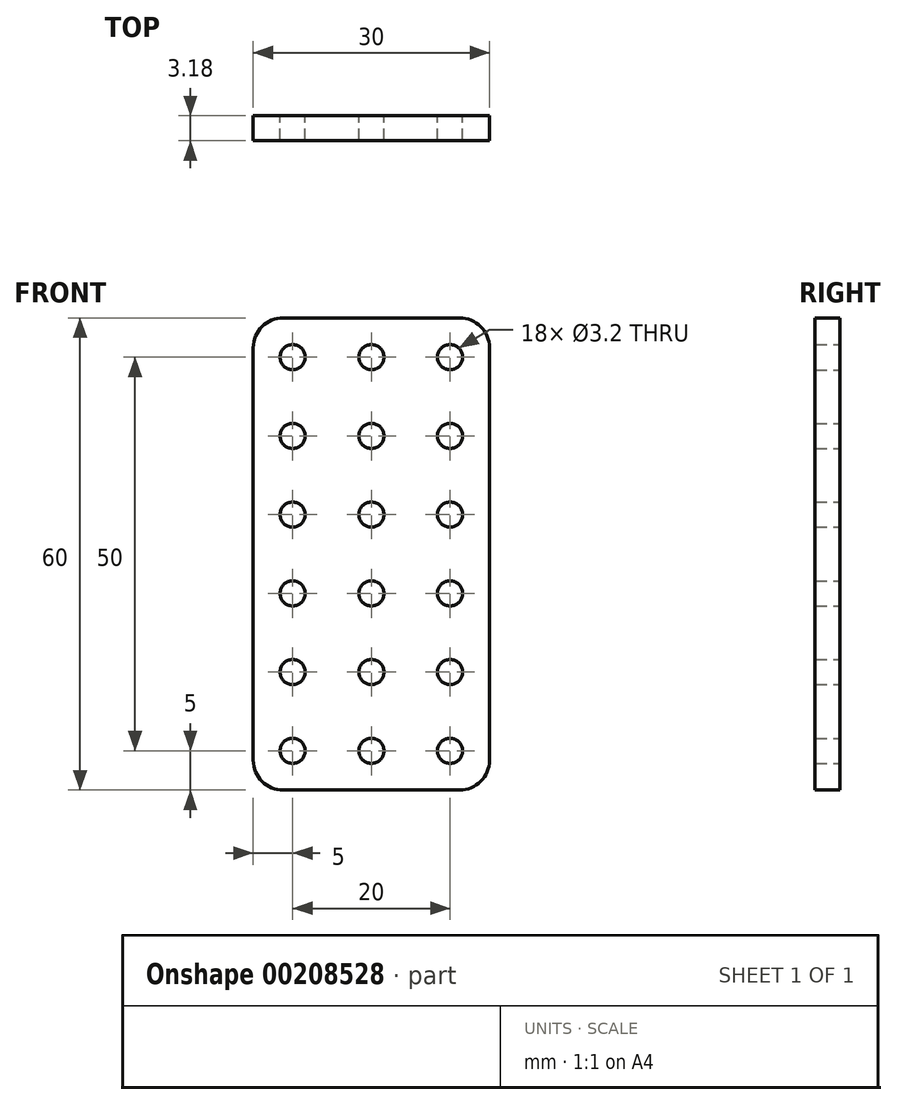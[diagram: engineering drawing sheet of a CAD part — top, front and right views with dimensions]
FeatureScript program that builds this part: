
annotation { "Feature Type Name" : "Feature", "Feature Type Description" : "" }
export const myFeature = defineFeature(function(context is Context, id is Id, definition is map)
    precondition{}
    {
        {
            var Q0;
            Q0=qCreatedBy(makeId("Front.planeOp"),FACE);
            var sketch = newSketch(context, id + "F0", { "sketchPlane" : qUnion([Q0])});
            skLineSegment(sketch, "E0.bottom", {"start": v(3.8, 0) * mm, "end": v(26.19, 0) * mm});
            skLineSegment(sketch, "E0.top", {"start": v(3.81, -60) * mm, "end": v(26.19, -60) * mm});
            skLineSegment(sketch, "E0.left", {"start": v(0, -3.81) * mm, "end": v(0, -56.19) * mm});
            skLineSegment(sketch, "E0.right", {"start": v(30, -3.81) * mm, "end": v(30, -56.19) * mm});
            skCircle(sketch, "E1", {"center": v(5, -5) * mm, "radius": 1.6 * mm});
            skCircle(sketch, "E2.0.1.0", {"center": v(5, -15) * mm, "radius": 1.6 * mm});
            skCircle(sketch, "E2.0.2.0", {"center": v(5, -25) * mm, "radius": 1.6 * mm});
            skCircle(sketch, "E2.0.3.0", {"center": v(5, -35) * mm, "radius": 1.6 * mm});
            skCircle(sketch, "E2.0.4.0", {"center": v(5, -45) * mm, "radius": 1.6 * mm});
            skCircle(sketch, "E2.0.5.0", {"center": v(5, -55) * mm, "radius": 1.6 * mm});
            skCircle(sketch, "E2.1.0.0", {"center": v(15, -5) * mm, "radius": 1.6 * mm});
            skCircle(sketch, "E2.1.1.0", {"center": v(15, -15) * mm, "radius": 1.6 * mm});
            skCircle(sketch, "E2.1.2.0", {"center": v(15, -25) * mm, "radius": 1.6 * mm});
            skCircle(sketch, "E2.1.3.0", {"center": v(15, -35) * mm, "radius": 1.6 * mm});
            skCircle(sketch, "E2.1.4.0", {"center": v(15, -45) * mm, "radius": 1.6 * mm});
            skCircle(sketch, "E2.1.5.0", {"center": v(15, -55) * mm, "radius": 1.6 * mm});
            skCircle(sketch, "E2.2.0.0", {"center": v(25, -5) * mm, "radius": 1.6 * mm});
            skCircle(sketch, "E2.2.1.0", {"center": v(25, -15) * mm, "radius": 1.6 * mm});
            skCircle(sketch, "E2.2.2.0", {"center": v(25, -25) * mm, "radius": 1.6 * mm});
            skCircle(sketch, "E2.2.3.0", {"center": v(25, -35) * mm, "radius": 1.6 * mm});
            skCircle(sketch, "E2.2.4.0", {"center": v(25, -45) * mm, "radius": 1.6 * mm});
            skCircle(sketch, "E2.2.5.0", {"center": v(25, -55) * mm, "radius": 1.6 * mm});
            skLineSegment(sketch, "E2.direction1", {"start": v(5, -5) * mm, "end": v(15, -5) * mm, "construction": true});
            skLineSegment(sketch, "E2.direction2", {"start": v(5, -5) * mm, "end": v(5, -15) * mm, "construction": true});
            skPoint(sketch, "E3.visualSharp", {"position": v(0, 0) * mm});
            skArc(sketch, "E3.filletArc", {"start": v(3.8, 0) * mm, "mid": v(1.12, -1.12) * mm, "end": v(0, -3.81) * mm});
            skPoint(sketch, "E4.visualSharp", {"position": v(30, 0) * mm});
            skArc(sketch, "E4.filletArc", {"start": v(30, -3.81) * mm, "mid": v(28.88, -1.12) * mm, "end": v(26.19, 0) * mm});
            skPoint(sketch, "E5.visualSharp", {"position": v(0, -60) * mm});
            skArc(sketch, "E5.filletArc", {"start": v(0, -56.19) * mm, "mid": v(1.12, -58.88) * mm, "end": v(3.81, -60) * mm});
            skPoint(sketch, "E6.visualSharp", {"position": v(30, -60) * mm});
            skArc(sketch, "E6.filletArc", {"start": v(26.19, -60) * mm, "mid": v(28.88, -58.88) * mm, "end": v(30, -56.19) * mm});
            skSolve(sketch);
        }
        {
            var Q0;
            Q0=makeQuery(id+"F0.imprint","IMPRINT",FACE,{"disambiguationData":[TD([[makeQuery(id+"F0.imprint","IMPRINT",EDGE,{"derivedFrom":sQuery(id+"F0.wireOp",EDGE,"E0.bottom")}),-1.0]])]});
            extrude(context, id + "F1", {"entities" : qUnion([Q0]), "depth" : 3.17 * mm});
        }
    });
